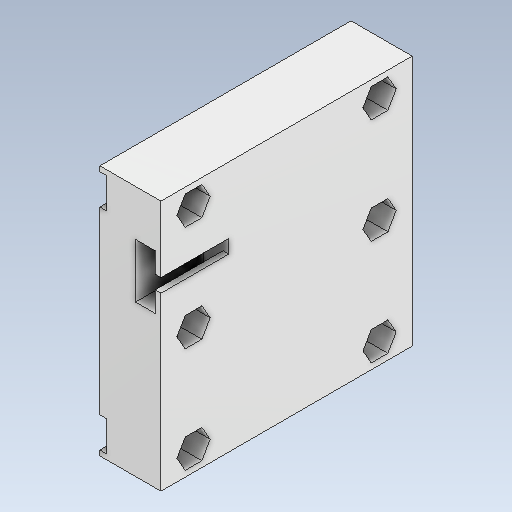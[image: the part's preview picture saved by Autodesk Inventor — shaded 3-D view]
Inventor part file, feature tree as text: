
AUTODESK INVENTOR PART (.ipt)
format: ipt  version: 2020 (Build 240168000, 168)  size: 229,888 bytes
history: native  units: mm
features: extrude x5, sketch x4, other x1, projected_geometry x1
ambient origin geometry x8: Origin, YZ Plane, XZ Plane, XY Plane, X Axis, Y Axis, Z Axis, Center Point
bodies: Body1 (feature_tree)
feature tree (11):
  other  "Bryła1"
  extrude  "Wyciągnięcie proste1"  Depth=74.0mm
  sketch  "Szkic2"
  extrude  "Wyciągnięcie proste2"  Depth=74.0mm
  extrude  "Wyciągnięcie proste3"  Depth=18.0mm TaperAngle=0.0deg
  extrude  "Wyciągnięcie proste4"  Depth=6.0mm
  extrude  "Wyciągnięcie proste5"  Depth=5.7mm
  sketch  "Szkic1"
  sketch  "Szkic3"
  sketch  "Szkic4"
  projected_geometry  "Pętla rzutowana1"
